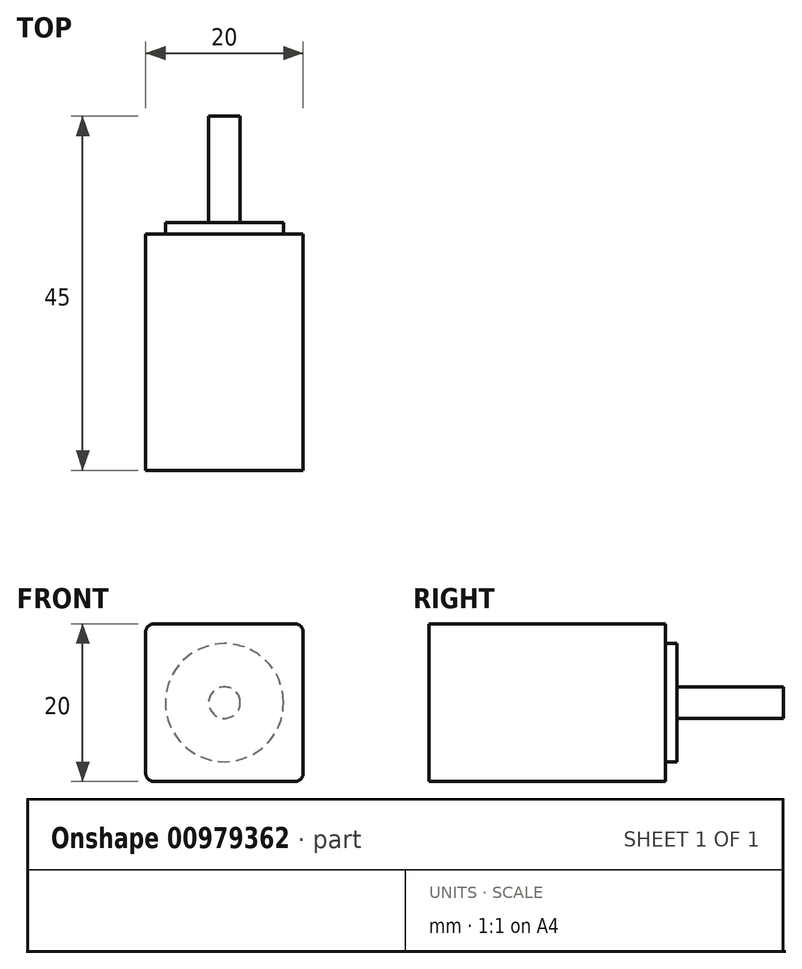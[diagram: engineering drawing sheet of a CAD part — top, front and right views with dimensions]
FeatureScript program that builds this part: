
annotation { "Feature Type Name" : "Feature", "Feature Type Description" : "" }
export const myFeature = defineFeature(function(context is Context, id is Id, definition is map)
    precondition{}
    {
        {
            var Q0;
            Q0=qCreatedBy(makeId("Front.planeOp"),FACE);
            var sketch = newSketch(context, id + "F0", { "sketchPlane" : qUnion([Q0])});
            skLineSegment(sketch, "E0.bottom", {"start": v(-10, 10) * mm, "end": v(10, 10) * mm});
            skLineSegment(sketch, "E0.top", {"start": v(-10, -10) * mm, "end": v(10, -10) * mm});
            skLineSegment(sketch, "E0.left", {"start": v(-10, 10) * mm, "end": v(-10, -10) * mm});
            skLineSegment(sketch, "E0.right", {"start": v(10, 10) * mm, "end": v(10, -10) * mm});
            skCircle(sketch, "E1", {"center": v(0, 0) * mm, "radius": 2 * mm});
            skCircle(sketch, "E2", {"center": v(0, 0) * mm, "radius": 7.5 * mm});
            skSolve(sketch);
        }
        {
            var Q0;
            Q0=makeQuery(id+"F0.imprint","IMPRINT",FACE,{"disambiguationData":[TD([[makeQuery(id+"F0.imprint","IMPRINT",EDGE,{"derivedFrom":sQuery(id+"F0.wireOp",EDGE,"E0.bottom")}),-1.0]])]});
            var Q1;
            Q1=makeQuery(id+"F0.imprint","IMPRINT",FACE,{"disambiguationData":[TD([[makeQuery(id+"F0.imprint","IMPRINT",EDGE,{"derivedFrom":sQuery(id+"F0.wireOp",EDGE,"E1")}),1.0]])]});
            var Q2;
            Q2=makeQuery(id+"F0.imprint","IMPRINT",FACE,{"disambiguationData":[TD([[makeQuery(id+"F0.imprint","IMPRINT",EDGE,{"derivedFrom":sQuery(id+"F0.wireOp",EDGE,"E1")}),-1.0]])]});
            extrude(context, id + "F1", {"entities" : qUnion([Q0, Q1, Q2]), "depth" : 30 * mm, "offsetDistance" : 25 * mm});
        }
        {
            var Q0;
            Q0=makeQuery(id+"F0.imprint","IMPRINT",FACE,{"disambiguationData":[TD([[makeQuery(id+"F0.imprint","IMPRINT",EDGE,{"derivedFrom":sQuery(id+"F0.wireOp",EDGE,"E1")}),1.0]])]});
            extrude(context, id + "F2", {"entities" : qUnion([Q0]), "operationType" : NewBodyOperationType.ADD, "oppositeDirection" : true, "depth" : 15 * mm, "offsetDistance" : 25 * mm});
        }
        {
            var Q0;
            Q0=makeQuery(id+"F1.opExtrude","SWEPT_EDGE",EDGE,{"disambiguationData":[OSD([sQuery(id+"F0.wireOp",EDGE,"E0.bottom"),sQuery(id+"F0.wireOp",EDGE,"E0.right")])]});
            var Q1;
            Q1=makeQuery(id+"F1.opExtrude","SWEPT_EDGE",EDGE,{"disambiguationData":[OSD([sQuery(id+"F0.wireOp",EDGE,"E0.bottom"),sQuery(id+"F0.wireOp",EDGE,"E0.left")])]});
            var Q2;
            Q2=makeQuery(id+"F1.opExtrude","SWEPT_EDGE",EDGE,{"disambiguationData":[OSD([sQuery(id+"F0.wireOp",EDGE,"E0.top"),sQuery(id+"F0.wireOp",EDGE,"E0.left")])]});
            var Q3;
            Q3=makeQuery(id+"F1.opExtrude","SWEPT_EDGE",EDGE,{"disambiguationData":[OSD([sQuery(id+"F0.wireOp",EDGE,"E0.top"),sQuery(id+"F0.wireOp",EDGE,"E0.right")])]});
            fillet(context, id + "F3", {"entities" : qUnion([Q0, Q1, Q2, Q3]), "radius" : 1 * mm, "tangentPropagation" : true, "allowEdgeOverflow" : false});
        }
        {
            var Q0;
            Q0=makeQuery(id+"F0.imprint","IMPRINT",FACE,{"disambiguationData":[TD([[makeQuery(id+"F0.imprint","IMPRINT",EDGE,{"derivedFrom":sQuery(id+"F0.wireOp",EDGE,"E1")}),-1.0]])]});
            extrude(context, id + "F4", {"entities" : qUnion([Q0]), "operationType" : NewBodyOperationType.ADD, "oppositeDirection" : true, "depth" : 1.5 * mm, "offsetDistance" : 25 * mm});
        }
    });
